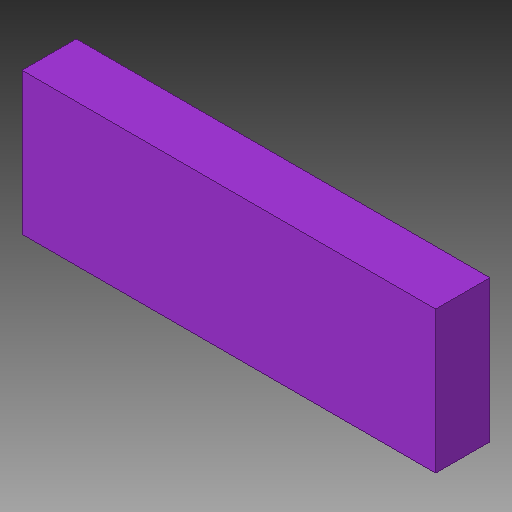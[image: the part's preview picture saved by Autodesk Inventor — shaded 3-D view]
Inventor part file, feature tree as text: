
AUTODESK INVENTOR PART (.ipt)
format: ipt  version: 2018 (Build 220112000, 112)  size: 80,896 bytes
history: native  units: in
note: dims shown in document units (in); Inventor stores cm internally (conversion verified against a paired STEP export)
features: other x1, extrude x1
ambient origin geometry x8: Origin, YZ Plane, XZ Plane, XY Plane, X Axis, Y Axis, Z Axis, Center Point
bodies: Solid1 (feature_tree)
feature tree (2):
  other  "1X03, 1X03_53"
  extrude  "Extrusion1"  Depth=0.0394in TaperAngle=0.0deg
